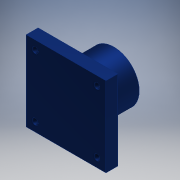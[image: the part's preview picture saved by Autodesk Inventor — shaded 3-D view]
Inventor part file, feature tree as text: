
AUTODESK INVENTOR PART (.ipt)
format: ipt  version: 2018 (Build 220112000, 112)  size: 121,856 bytes
history: native  units: mm
features: sketch x4, extrude x2, hole x2, other x1
ambient origin geometry x8: Origin, YZ Plane, XZ Plane, XY Plane, X Axis, Y Axis, Z Axis, Center Point
bodies: Body1 (feature_tree)
feature tree (9):
  other  "Sólido1"
  extrude  "Extrusión1"  Depth=40.0mm
  hole  "Agujero1"  [1 undecoded]
  extrude  "Extrusión2"  Depth=8.0mm
  hole  "Agujero2"  [1 undecoded]
  sketch  "Boceto1"  dims[d0=40.0mm d1=40.0mm]
  sketch  "Boceto2"  dims[d2=6.0mm d3=0.0mm d4=31.0mm]
  sketch  "Boceto3"  dims[d5=31.0mm]
  sketch  "Boceto4"  dims[d6=3.0mm d7=6.0mm d8=4.0mm d9=2.0mm d10=90.0deg d11=8.0mm d12=20.594885mm d13=25.4mm d14=18.0mm d15=0.0mm d16=12.0mm d17=6.0mm d18=4.0mm d19=2.0mm d20=90.0deg d21=8.0mm d22=0.0mm]
note: 2 required parameter values undecoded (feature->parameter linkage not recoverable at this tier; creation-order binding heuristic only, values carry confidence <= 0.55)
